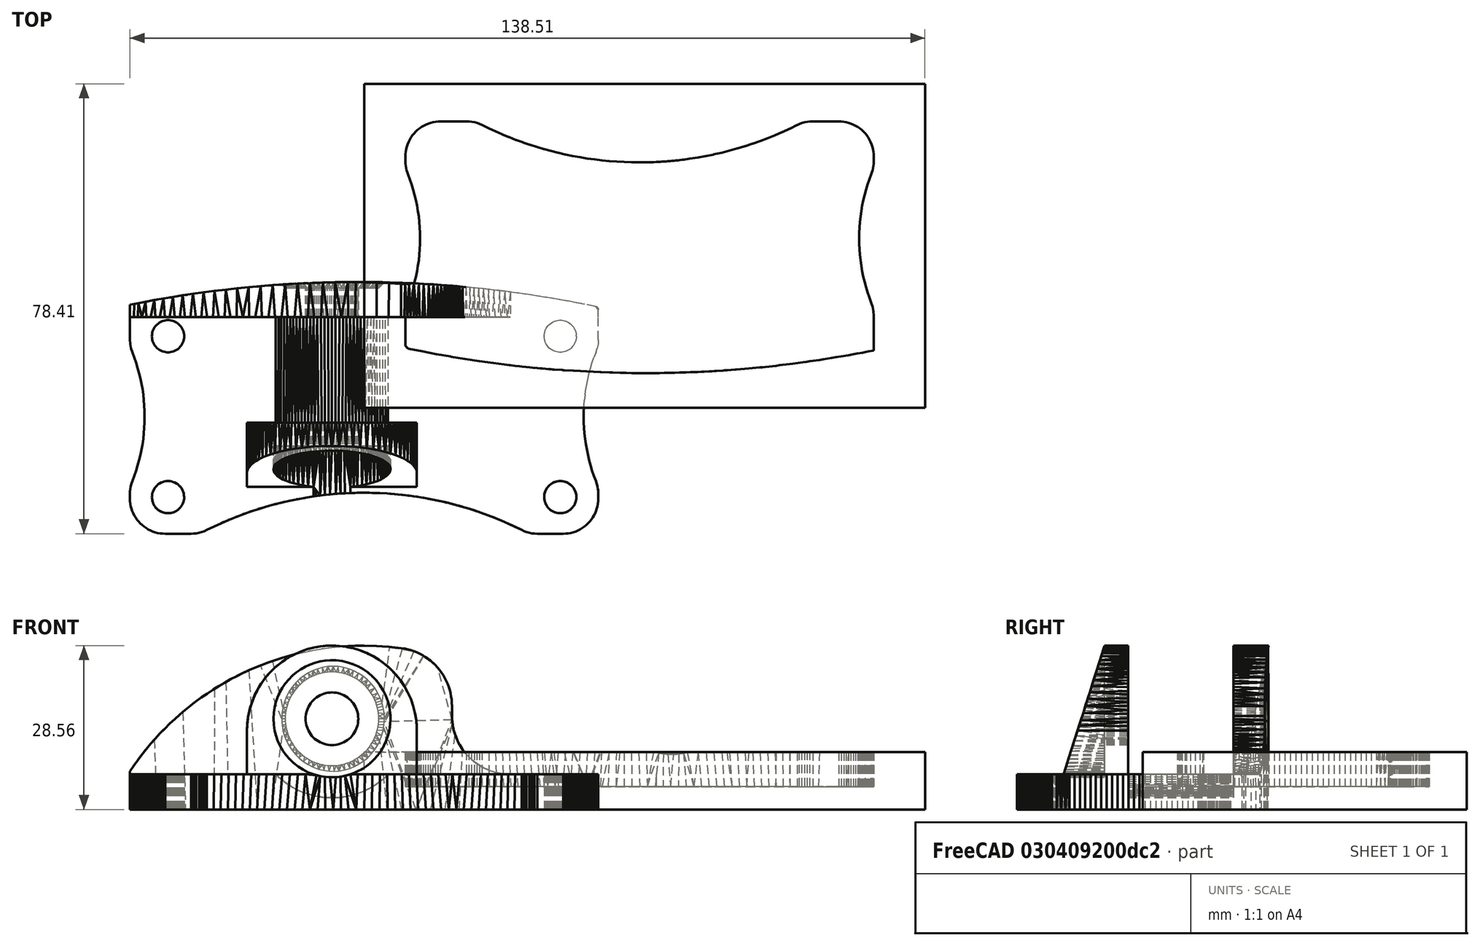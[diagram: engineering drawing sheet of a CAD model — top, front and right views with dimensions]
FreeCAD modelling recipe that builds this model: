
FCSTD DOCUMENT  (FreeCAD 0.17R9537 (Git))
Label: Y_idler_insert_jig
License: All rights reserved
LicenseURL: http://en.wikipedia.org/wiki/All_rights_reserved
objects: Part::Feature×4, Sketcher::SketchObject×2, PartDesign::Body×2, Mesh::Feature×1, PartDesign::Pad×1, Part::Cut×1, PartDesign::Pocket×1, PartDesign::Fillet×1
note: 14 computed .brp shape members not serialized (recipe doc carries the construction recipe); baked Part::Feature solids carry a one-line shape summary decoded from their .brp

FEATURE [Sketcher::SketchObject] Sketch
  MapMode = 5
  Support = -> [XY_Plane]
  sketch-geometry (4):
    g0: LineSegment StartX=0 StartY=0 StartZ=0 EndX=97.711 EndY=0 EndZ=0
    g1: LineSegment StartX=97.711 StartY=0 StartZ=0 EndX=97.711 EndY=56.4735 EndZ=0
    g2: LineSegment StartX=97.711 StartY=56.4735 StartZ=0 EndX=0 EndY=56.4735 EndZ=0
    g3: LineSegment StartX=0 StartY=56.4735 StartZ=0 EndX=0 EndY=0 EndZ=0
  constraints (9):
    c: Coincident(g0,g1)
    c: Coincident(g1,g2)
    c: Coincident(g2,g3)
    c: Coincident(g3,g0)
    c: Horizontal(g0)
    c: Horizontal(g2)
    c: Vertical(g1)
    c: Vertical(g3)
    c: Coincident(g0,g-1)
FEATURE [Mesh::Feature] y_idler_taz_2_larger  label="y_idler_taz_2%larger"
FEATURE [Part::Feature] y_idler_taz_2_larger001
  shape: bbox 81.6 x 43.87 x 28.56 mm, 4478 faces, 0 solids (baked)
FEATURE [Part::Feature] y_idler_taz_2_larger001_solid  label="y_idler_taz_2_larger001 (Solid)"
  shape: bbox 81.6 x 43.87 x 28.56 mm, 4478 faces (baked)
FEATURE [Part::Feature] y_idler_taz_2_larger001_solid001  label="y_idler_taz_2_larger001 (Solid)001"
  Placement = pos=(48,28,4) rot=(0,0,-1;3.14159rad)
  shape: bbox 81.6 x 43.87 x 28.56 mm, 1746 faces (baked)
FEATURE [PartDesign::Pad] Pad
  Length = 10
  Length2 = 100
  Profile = -> Sketch
  Type = 0
FEATURE [PartDesign::Body] Body
  Model = -> [Sketch,Pad]
  Origin = -> BodyOrigin
  Tip = -> Pad
FEATURE [Part::Cut] Cut
  Base = -> Pad
  Tool = -> y_idler_taz_2_larger001_solid001
FEATURE [Sketcher::SketchObject] Sketch001
  ExternalGeometry = -> [Cut]
  MapMode = 5
  Placement = pos=(0,0,4) rot=(0,0,1;0rad)
  Support = -> [Cut]
  sketch-geometry (11):
    g0: Circle CenterX=13.6357 CenterY=43.4953 CenterZ=0 NormalX=0 NormalY=0 NormalZ=1 Radius=4.36424
    g1: Circle CenterX=14.106 CenterY=15.4666 CenterZ=0 NormalX=0 NormalY=0 NormalZ=1 Radius=4.45651
    g2: Circle CenterX=82.2966 CenterY=15.4666 CenterZ=0 NormalX=0 NormalY=0 NormalZ=1 Radius=4.35713
    g3: Circle CenterX=82.3906 CenterY=43.4953 CenterZ=0 NormalX=0 NormalY=0 NormalZ=1 Radius=4.54982
    g4: ArcOfCircle CenterX=49.0206 CenterY=93.0792 CenterZ=0 NormalX=0 NormalY=0 NormalZ=1 Radius=50.2475 StartAngle=4.74893 EndAngle=4.85968
    g5: LineSegment StartX=56.3948 StartY=43.3757 StartZ=0 EndX=63.5801 EndY=32.7817 EndZ=0
    g6: LineSegment StartX=50.8561 StartY=42.8652 StartZ=0 EndX=44.6453 EndY=35.7715 EndZ=0
    g7: LineSegment StartX=44.6453 StartY=35.7715 StartZ=0 EndX=36.9279 EndY=13.8823 EndZ=0
    g8: LineSegment StartX=36.9279 StartY=13.8823 StartZ=0 EndX=49.9772 EndY=8.83098 EndZ=0
    g9: LineSegment StartX=49.9772 StartY=8.83098 StartZ=0 EndX=65.8329 EndY=10.0938 EndZ=0
    g10: LineSegment StartX=65.8329 StartY=10.0938 StartZ=0 EndX=63.5801 EndY=32.7817 EndZ=0
  constraints (9):
    c: Coincident(g4,g-3)
    c: Coincident(g4,g-4)
    c: Coincident(g5,g4)
    c: Coincident(g6,g4)
    c: Coincident(g7,g6)
    c: Coincident(g8,g7)
    c: Coincident(g9,g8)
    c: Coincident(g10,g9)
    c: Coincident(g10,g5)
FEATURE [PartDesign::Pocket] Pocket
  BaseFeature = -> Cut
  Length = 5
  Profile = -> Sketch001
  Reversed = true
  Type = 1
FEATURE [PartDesign::Body] Body001
  BaseFeature = -> Cut
  Model = -> [Sketch001,Pocket]
  Origin = -> Body001Origin
  Tip = -> Pocket
FEATURE [Part::Feature] Body001001  label="Body002"
  shape: bbox 97.71 x 56.47 x 10 mm, 357 faces (baked)
FEATURE [PartDesign::Fillet] Fillet
  Base = -> Body001001 [Edge32,Edge29,Edge25,Edge26]
  Radius = 7
